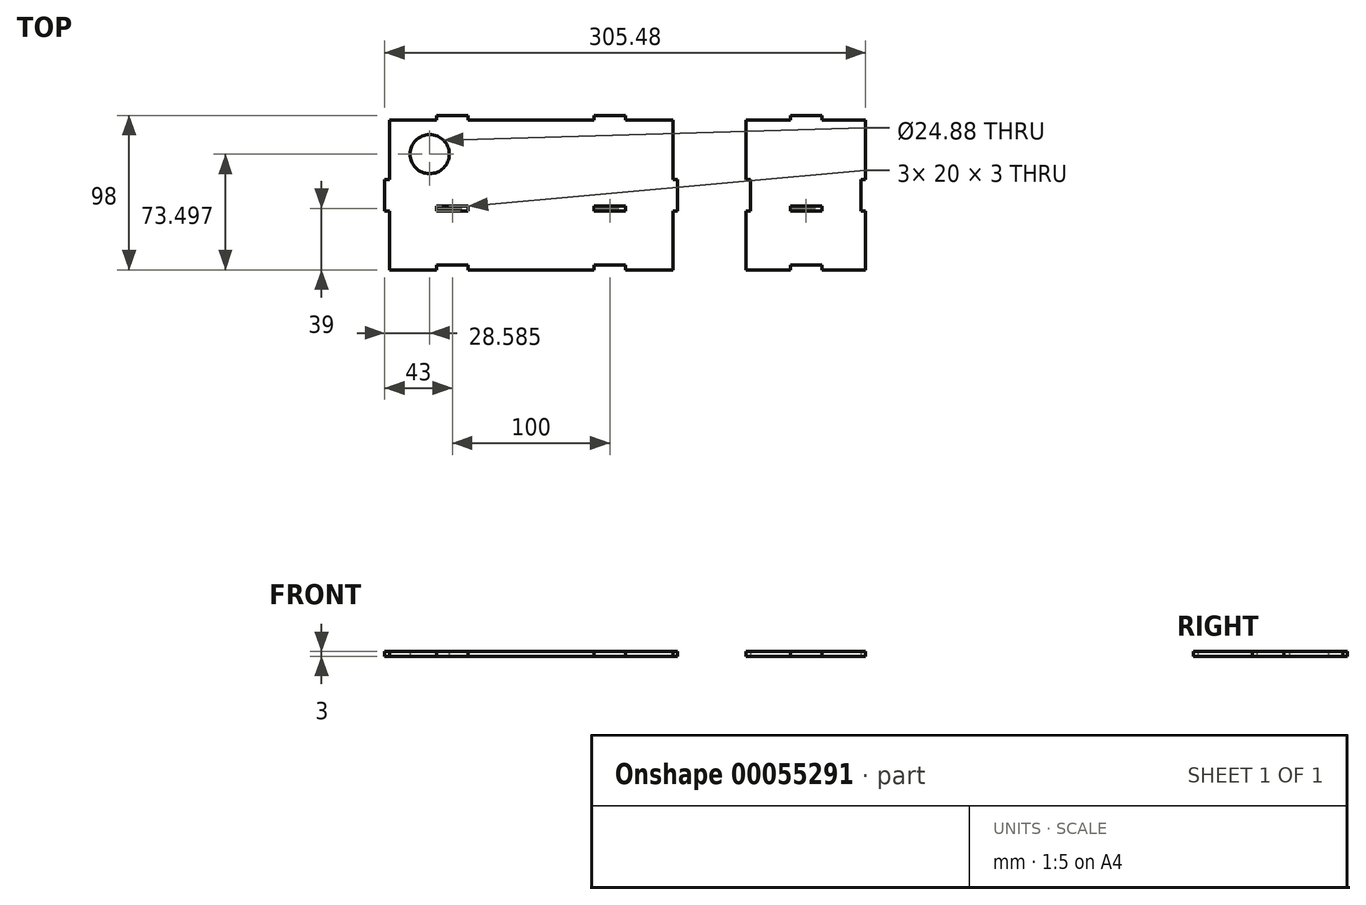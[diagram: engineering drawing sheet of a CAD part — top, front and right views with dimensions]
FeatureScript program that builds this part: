
annotation { "Feature Type Name" : "Feature", "Feature Type Description" : "" }
export const myFeature = defineFeature(function(context is Context, id is Id, definition is map)
    precondition{}
    {
        {
            assignVariable(context, id + "F0", {"name" : "PanelThickness", "anyValue" : 3});
        }
        {
            var Q0;
            Q0=qCreatedBy(makeId("Top.planeOp"),FACE);
            var sketch = newSketch(context, id + "F1", { "sketchPlane" : qUnion([Q0])});
            skPoint(sketch, "E0.0", {"position": v(-90, 47.5) * mm});
            skLineSegment(sketch, "E1", {"start": v(-90, -47.5) * mm, "end": v(-60, -47.5) * mm});
            skLineSegment(sketch, "E2", {"start": v(-40, -47.5) * mm, "end": v(40, -47.5) * mm});
            skLineSegment(sketch, "E3", {"start": v(40, -44.5) * mm, "end": v(60, -44.5) * mm});
            skLineSegment(sketch, "E4", {"start": v(60, -47.5) * mm, "end": v(90, -47.5) * mm});
            skLineSegment(sketch, "E5", {"start": v(90, 47.5) * mm, "end": v(90, -10) * mm});
            skLineSegment(sketch, "E6", {"start": v(-90, -47.5) * mm, "end": v(-90, 47.5) * mm});
            skLineSegment(sketch, "E7", {"start": v(-90, 47.5) * mm, "end": v(-60, 47.5) * mm});
            skLineSegment(sketch, "E8", {"start": v(-60, 50.5) * mm, "end": v(-40, 50.5) * mm});
            skLineSegment(sketch, "E9", {"start": v(40, 50.5) * mm, "end": v(60, 50.5) * mm});
            skLineSegment(sketch, "E10", {"start": v(60, 47.5) * mm, "end": v(90, 47.5) * mm});
            skLineSegment(sketch, "E11", {"start": v(-40, 47.5) * mm, "end": v(40, 47.5) * mm});
            skLineSegment(sketch, "E12", {"start": v(60, 47.5) * mm, "end": v(60, 50.5) * mm});
            skLineSegment(sketch, "E13", {"start": v(40, 47.5) * mm, "end": v(40, 50.5) * mm});
            skLineSegment(sketch, "E14", {"start": v(-40, 47.5) * mm, "end": v(-40, 50.5) * mm});
            skLineSegment(sketch, "E15", {"start": v(-60, 47.5) * mm, "end": v(-60, 50.5) * mm});
            skLineSegment(sketch, "E16", {"start": v(40, -47.5) * mm, "end": v(40, -44.5) * mm});
            skLineSegment(sketch, "E17", {"start": v(60, -47.5) * mm, "end": v(60, -44.5) * mm});
            skLineSegment(sketch, "E18", {"start": v(-60, -44.5) * mm, "end": v(-40, -44.5) * mm});
            skLineSegment(sketch, "E19", {"start": v(-40, -47.5) * mm, "end": v(-40, -44.5) * mm});
            skLineSegment(sketch, "E20", {"start": v(-60, -47.5) * mm, "end": v(-60, -44.5) * mm});
            skLineSegment(sketch, "E21.top", {"start": v(90, 10) * mm, "end": v(93, 10) * mm});
            skLineSegment(sketch, "E22.top", {"start": v(90, -10) * mm, "end": v(93, -10) * mm});
            skLineSegment(sketch, "E23", {"start": v(0, -47.5) * mm, "end": v(0, 47.5) * mm, "construction": true});
            skLineSegment(sketch, "E24.0", {"start": v(-60, -7) * mm, "end": v(-60, -10) * mm});
            skLineSegment(sketch, "E24.1", {"start": v(-40, -7) * mm, "end": v(-60, -7) * mm});
            skLineSegment(sketch, "E24.2", {"start": v(-40, -7) * mm, "end": v(-40, -10) * mm});
            skLineSegment(sketch, "E24.3", {"start": v(-40, -10) * mm, "end": v(-60, -10) * mm});
            skLineSegment(sketch, "E24.4", {"start": v(40, -7) * mm, "end": v(40, -10) * mm});
            skLineSegment(sketch, "E24.5", {"start": v(40, -7) * mm, "end": v(60, -7) * mm});
            skLineSegment(sketch, "E24.6", {"start": v(40, -10) * mm, "end": v(60, -10) * mm});
            skLineSegment(sketch, "E24.7", {"start": v(60, -7) * mm, "end": v(60, -10) * mm});
            skLineSegment(sketch, "E25", {"start": v(90, -10) * mm, "end": v(90, -47.5) * mm});
            skLineSegment(sketch, "E26.0", {"start": v(93, 163.25) * mm, "end": v(93, 87.25) * mm, "construction": true});
            skLineSegment(sketch, "E27.0", {"start": v(93, 163.25) * mm, "end": v(-93, 163.25) * mm, "construction": true});
            skPoint(sketch, "E28.rect.middle", {"position": v(0, 125.25) * mm});
            skLineSegment(sketch, "E29.MirrorCS", {"start": v(40, 163.25) * mm, "end": v(60, 163.25) * mm});
            skLineSegment(sketch, "E28.rect.bottom", {"start": v(90, 160.25) * mm, "end": v(-90, 160.25) * mm});
            skLineSegment(sketch, "E28.rect.top", {"start": v(90, 90.25) * mm, "end": v(-90, 90.25) * mm});
            skLineSegment(sketch, "E28.rect.left", {"start": v(90, 160.25) * mm, "end": v(90, 90.25) * mm});
            skLineSegment(sketch, "E28.rect.right", {"start": v(-90, 160.25) * mm, "end": v(-90, 90.25) * mm});
            skLineSegment(sketch, "E30.bottom", {"start": v(40, 90.25) * mm, "end": v(60, 90.25) * mm});
            skLineSegment(sketch, "E30.top", {"start": v(40, 87.25) * mm, "end": v(60, 87.25) * mm});
            skLineSegment(sketch, "E31.MirrorCS", {"start": v(-40, 87.25) * mm, "end": v(-60, 87.25) * mm});
            skLineSegment(sketch, "E32.MirrorCS", {"start": v(-40, 163.25) * mm, "end": v(-60, 163.25) * mm});
            skLineSegment(sketch, "E33.0", {"start": v(93, 87.25) * mm, "end": v(-93, 87.25) * mm, "construction": true});
            skLineSegment(sketch, "E34.0", {"start": v(-93, 163.25) * mm, "end": v(-93, 87.25) * mm, "construction": true});
            skLineSegment(sketch, "E35.MirrorCS", {"start": v(93, 115.51) * mm, "end": v(93, 135.51) * mm});
            skLineSegment(sketch, "E36.right", {"start": v(-93, 115.25) * mm, "end": v(-93, 135.25) * mm});
            skPoint(sketch, "E37", {"position": v(-93, 125.25) * mm});
            skLineSegment(sketch, "E38.MirrorCS", {"start": v(90, 115.51) * mm, "end": v(93, 115.51) * mm});
            skLineSegment(sketch, "E36.left", {"start": v(-90, 115.25) * mm, "end": v(-90, 135.25) * mm});
            skLineSegment(sketch, "E39.MirrorCS", {"start": v(-60, 160.25) * mm, "end": v(-60, 163.25) * mm});
            skLineSegment(sketch, "E40.MirrorCS", {"start": v(40, 160.25) * mm, "end": v(40, 163.25) * mm});
            skLineSegment(sketch, "E41.MirrorCS", {"start": v(-40, 90.25) * mm, "end": v(-40, 87.25) * mm});
            skLineSegment(sketch, "E42.MirrorCS", {"start": v(-60, 90.25) * mm, "end": v(-60, 87.25) * mm});
            skLineSegment(sketch, "E43.MirrorCS", {"start": v(-40, 160.25) * mm, "end": v(-40, 163.25) * mm});
            skLineSegment(sketch, "E44.MirrorCS", {"start": v(90, 135.51) * mm, "end": v(93, 135.51) * mm});
            skLineSegment(sketch, "E45.MirrorCS", {"start": v(60, 160.25) * mm, "end": v(60, 163.25) * mm});
            skLineSegment(sketch, "E36.bottom", {"start": v(-90, 115.25) * mm, "end": v(-93, 115.25) * mm});
            skLineSegment(sketch, "E30.left", {"start": v(40, 90.25) * mm, "end": v(40, 87.25) * mm});
            skLineSegment(sketch, "E30.right", {"start": v(60, 90.25) * mm, "end": v(60, 87.25) * mm});
            skLineSegment(sketch, "E36.top", {"start": v(-90, 135.25) * mm, "end": v(-93, 135.25) * mm});
            skLineSegment(sketch, "E46", {"start": v(-60, 50.5) * mm, "end": v(-60, -67.68) * mm, "construction": true});
            skLineSegment(sketch, "E47", {"start": v(-40, 50.5) * mm, "end": v(-40, -72.3) * mm, "construction": true});
            skLineSegment(sketch, "E48", {"start": v(40, 47.5) * mm, "end": v(40, -61.26) * mm, "construction": true});
            skLineSegment(sketch, "E49", {"start": v(60, 47.5) * mm, "end": v(60, -68.98) * mm, "construction": true});
            skLineSegment(sketch, "E50.right", {"start": v(209.48, -10) * mm, "end": v(209.48, 10) * mm});
            skLineSegment(sketch, "E51", {"start": v(164.74, -44.5) * mm, "end": v(184.74, -44.5) * mm});
            skLineSegment(sketch, "E52", {"start": v(136.48, -47.5) * mm, "end": v(136.48, -10) * mm});
            skLineSegment(sketch, "E53", {"start": v(136.48, 47.5) * mm, "end": v(164.74, 47.5) * mm});
            skLineSegment(sketch, "E54", {"start": v(164.74, 50.5) * mm, "end": v(184.74, 50.5) * mm});
            skLineSegment(sketch, "E55", {"start": v(184.74, 47.5) * mm, "end": v(212.48, 47.5) * mm});
            skLineSegment(sketch, "E56", {"start": v(136.48, -10) * mm, "end": v(220.48, -10) * mm, "construction": true});
            skLineSegment(sketch, "E57", {"start": v(136.48, 10) * mm, "end": v(209.48, 10) * mm, "construction": true});
            skPoint(sketch, "E58.rect.middle", {"position": v(174.74, -8.5) * mm});
            skLineSegment(sketch, "E59", {"start": v(212.48, -47.5) * mm, "end": v(212.48, -10) * mm});
            skLineSegment(sketch, "E60.0", {"start": v(139.48, -10) * mm, "end": v(139.48, 10) * mm});
            skLineSegment(sketch, "E61", {"start": v(164.74, -44.5) * mm, "end": v(164.74, 47.5) * mm, "construction": true});
            skLineSegment(sketch, "E62", {"start": v(184.74, -44.5) * mm, "end": v(184.74, 47.5) * mm, "construction": true});
            skLineSegment(sketch, "E58.rect.bottom", {"start": v(184.74, -10) * mm, "end": v(164.74, -10) * mm});
            skLineSegment(sketch, "E58.rect.top", {"start": v(184.74, -7) * mm, "end": v(164.74, -7) * mm});
            skLineSegment(sketch, "E50.bottom", {"start": v(212.48, -10) * mm, "end": v(209.48, -10) * mm});
            skLineSegment(sketch, "E58.rect.left", {"start": v(184.74, -10) * mm, "end": v(184.74, -7) * mm});
            skLineSegment(sketch, "E58.rect.right", {"start": v(164.74, -10) * mm, "end": v(164.74, -7) * mm});
            skLineSegment(sketch, "E50.top", {"start": v(212.48, 10) * mm, "end": v(209.48, 10) * mm});
            skLineSegment(sketch, "E63.bottom", {"start": v(136.48, -10) * mm, "end": v(139.48, -10) * mm});
            skLineSegment(sketch, "E64", {"start": v(164.74, 50.5) * mm, "end": v(164.74, 47.5) * mm});
            skLineSegment(sketch, "E65", {"start": v(184.74, 50.5) * mm, "end": v(184.74, 47.5) * mm});
            skLineSegment(sketch, "E66", {"start": v(90, 47.5) * mm, "end": v(136.48, 47.5) * mm, "construction": true});
            skLineSegment(sketch, "E67", {"start": v(90, -47.5) * mm, "end": v(136.48, -47.5) * mm, "construction": true});
            skLineSegment(sketch, "E68", {"start": v(136.48, -10) * mm, "end": v(93, -10) * mm, "construction": true});
            skLineSegment(sketch, "E69", {"start": v(93, -10) * mm, "end": v(93, 10) * mm});
            skLineSegment(sketch, "E70", {"start": v(-93, 0) * mm, "end": v(247.51, 0) * mm, "construction": true});
            skLineSegment(sketch, "E71", {"start": v(164.74, -44.5) * mm, "end": v(164.74, -47.5) * mm});
            skLineSegment(sketch, "E72", {"start": v(164.74, -47.5) * mm, "end": v(136.48, -47.5) * mm});
            skLineSegment(sketch, "E73", {"start": v(184.74, -44.5) * mm, "end": v(184.74, -47.5) * mm});
            skLineSegment(sketch, "E74", {"start": v(184.74, -47.5) * mm, "end": v(212.48, -47.5) * mm});
            skLineSegment(sketch, "E75", {"start": v(-60, 50.5) * mm, "end": v(-60, 87.25) * mm, "construction": true});
            skLineSegment(sketch, "E76", {"start": v(136.48, 10) * mm, "end": v(136.48, 47.5) * mm});
            skLineSegment(sketch, "E77", {"start": v(212.48, 10) * mm, "end": v(212.48, 47.5) * mm});
            skLineSegment(sketch, "E78", {"start": v(90, -10) * mm, "end": v(-131.81, -10) * mm, "construction": true});
            skLineSegment(sketch, "E79", {"start": v(136.48, 10) * mm, "end": v(-134.87, 10) * mm, "construction": true});
            skLineSegment(sketch, "E80", {"start": v(-93, 10) * mm, "end": v(-90, 10) * mm});
            skLineSegment(sketch, "E81", {"start": v(-90, -10) * mm, "end": v(-93, -10) * mm});
            skLineSegment(sketch, "E82", {"start": v(-93, 10) * mm, "end": v(-93, -10) * mm});
            skLineSegment(sketch, "E83", {"start": v(136.48, 10) * mm, "end": v(139.48, 10) * mm});
            skCircle(sketch, "E84", {"center": v(-64.41, 26) * mm, "radius": 12.44 * mm});
            skPoint(sketch, "E85", {"position": v(-90, 0) * mm});
            skPoint(sketch, "E86", {"position": v(-93, 0) * mm});
            skLineSegment(sketch, "E87", {"start": v(136.48, 47.5) * mm, "end": v(136.48, 163.25) * mm, "construction": true});
            skLineSegment(sketch, "E88", {"start": v(93, 87.25) * mm, "end": v(136.48, 87.25) * mm, "construction": true});
            skLineSegment(sketch, "E89", {"start": v(93, 163.25) * mm, "end": v(233.49, 163.25) * mm, "construction": true});
            skLineSegment(sketch, "E90", {"start": v(212.48, 47.5) * mm, "end": v(212.48, 163.25) * mm, "construction": true});
            skLineSegment(sketch, "E91", {"start": v(209.48, 10) * mm, "end": v(209.48, 163.25) * mm, "construction": true});
            skLineSegment(sketch, "E92", {"start": v(90, 90.25) * mm, "end": v(212.48, 90.25) * mm, "construction": true});
            skLineSegment(sketch, "E93", {"start": v(136.48, 87.25) * mm, "end": v(212.48, 163.25) * mm, "construction": true});
            skLineSegment(sketch, "E94", {"start": v(93, 115.51) * mm, "end": v(164.74, 115.51) * mm, "construction": true});
            skLineSegment(sketch, "E95", {"start": v(93, 135.51) * mm, "end": v(184.74, 135.51) * mm, "construction": true});
            skLineSegment(sketch, "E96", {"start": v(90, 160.25) * mm, "end": v(209.48, 160.25) * mm, "construction": true});
            skLineSegment(sketch, "E97", {"start": v(139.48, 90.25) * mm, "end": v(139.48, 10) * mm, "construction": true});
            skLineSegment(sketch, "E98", {"start": v(164.74, 115.51) * mm, "end": v(164.74, 47.5) * mm, "construction": true});
            skLineSegment(sketch, "E99", {"start": v(184.74, 47.5) * mm, "end": v(164.74, 47.5) * mm, "construction": true});
            skLineSegment(sketch, "E100", {"start": v(184.74, 135.51) * mm, "end": v(184.74, 47.5) * mm, "construction": true});
            skLineSegment(sketch, "E101", {"start": v(209.48, 160.25) * mm, "end": v(209.48, -47.5) * mm, "construction": true});
            skLineSegment(sketch, "E102", {"start": v(212.48, 163.25) * mm, "end": v(212.48, -47.5) * mm, "construction": true});
            skSolve(sketch);
        }
        {
            var Q0;
            {var subQ1=sQuery(id+"F1.wireOp",EDGE,"E1");Q0=makeQuery(id+"F1.imprint","IMPRINT",FACE,{"disambiguationData":[TD([[makeQuery(id+"F1.imprint","IMPRINT",EDGE,{"derivedFrom":subQ1}),1.0]])]});}
            var Q1;
            {var subQ4=sQuery(id+"F1.wireOp",EDGE,"3b86b983-0263-44d0-8503-49f76be5f0d3.MirrorCS");Q1=makeQuery(id+"F1.imprint","IMPRINT",FACE,{"disambiguationData":[TD([[makeQuery(id+"F1.imprint","IMPRINT",EDGE,{"derivedFrom":subQ4}),-1.0]])]});}
            var Q2;
            {var subQ4=sQuery(id+"F1.wireOp",EDGE,"E22.bottom");Q2=makeQuery(id+"F1.imprint","IMPRINT",FACE,{"disambiguationData":[TD([[makeQuery(id+"F1.imprint","IMPRINT",EDGE,{"derivedFrom":subQ4}),-1.0]])]});}
            var Q3;
            Q3=makeQuery(id+"F1.imprint","IMPRINT",FACE,{"disambiguationData":[TD([[makeQuery(id+"F1.imprint","IMPRINT",EDGE,{"derivedFrom":sQuery(id+"F1.wireOp",EDGE,"E21.top")}),-1.0]])]});
            var Q4;
            {var subQ1=sQuery(id+"F1.wireOp",EDGE,"E80");Q4=makeQuery(id+"F1.imprint","IMPRINT",FACE,{"disambiguationData":[TD([[makeQuery(id+"F1.imprint","IMPRINT",EDGE,{"derivedFrom":subQ1}),-1.0]])]});}
            extrude(context, id + "F2", {"entities" : qUnion([Q0, Q1, Q2, Q3, Q4]), "depth" : (getVariable(context, 'PanelThickness')) * mm});
        }
        {
            var Q0;
            Q0=makeQuery(id+"F1.imprint","IMPRINT",FACE,{"disambiguationData":[TD([[makeQuery(id+"F1.imprint","IMPRINT",EDGE,{"derivedFrom":sQuery(id+"F1.wireOp",EDGE,"E50.right")}),1.0]])]});
            extrude(context, id + "F3", {"entities" : qUnion([Q0]), "depth" : (getVariable(context, 'PanelThickness')) * mm});
        }
    });
